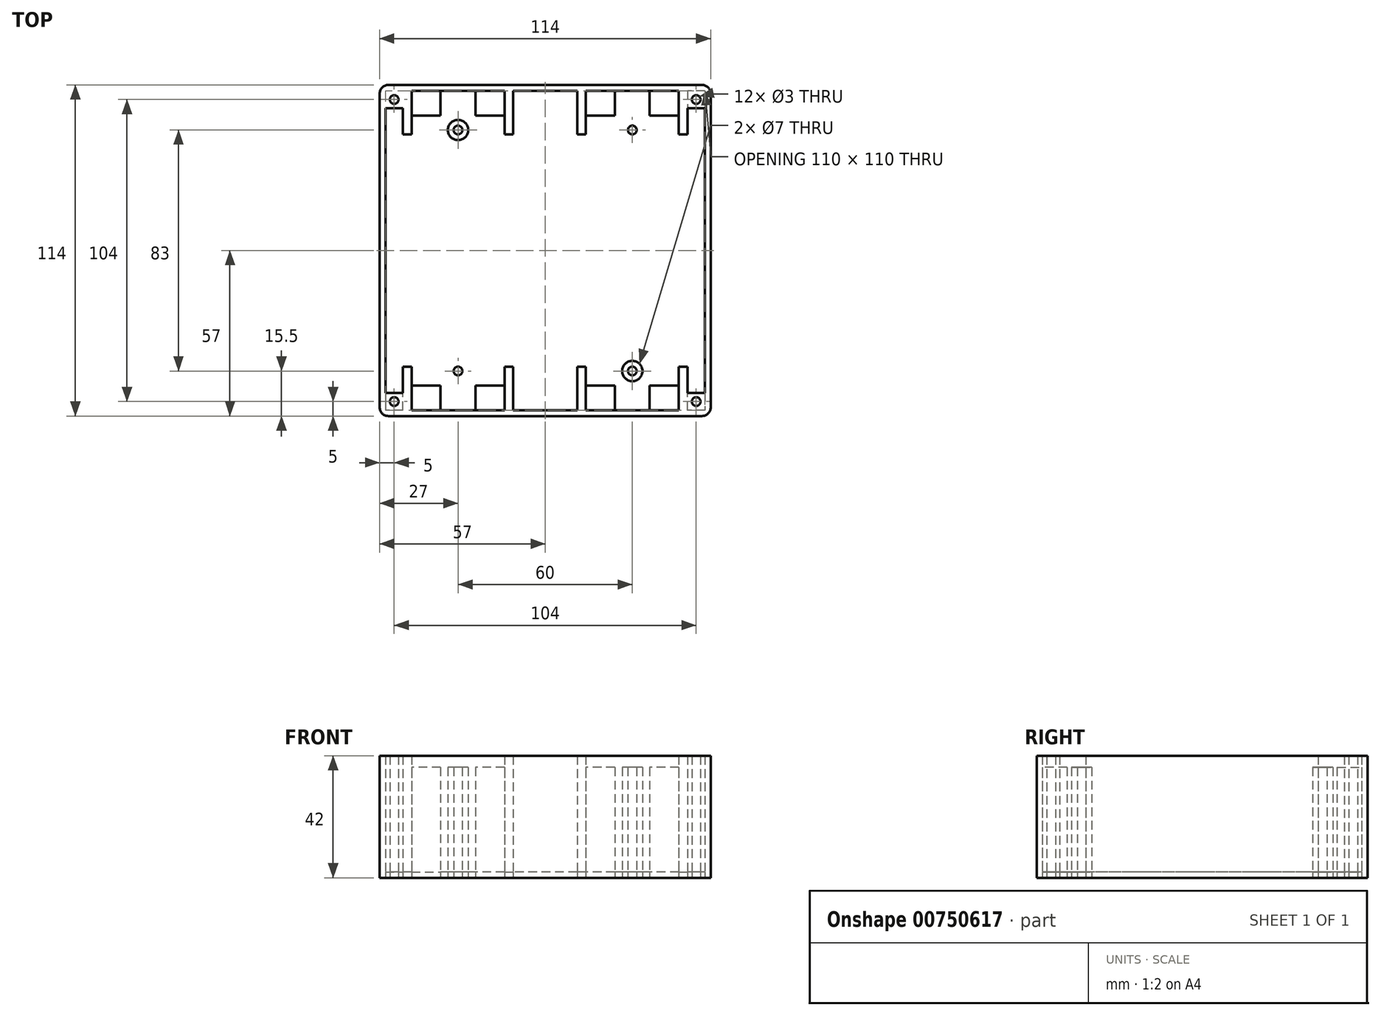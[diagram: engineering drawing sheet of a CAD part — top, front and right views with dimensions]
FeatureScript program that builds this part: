
annotation { "Feature Type Name" : "Feature", "Feature Type Description" : "" }
export const myFeature = defineFeature(function(context is Context, id is Id, definition is map)
    precondition{}
    {
        {
            var Q0;
            Q0=qCreatedBy(makeId("Top.planeOp"),FACE);
            var sketch = newSketch(context, id + "F0", { "sketchPlane" : qUnion([Q0])});
            skLineSegment(sketch, "E0.bottom", {"start": v(55, 55) * mm, "end": v(-55, 55) * mm});
            skLineSegment(sketch, "E0.top", {"start": v(55, -55) * mm, "end": v(-55, -55) * mm});
            skLineSegment(sketch, "E0.left", {"start": v(55, 55) * mm, "end": v(55, -55) * mm});
            skLineSegment(sketch, "E0.right", {"start": v(-55, 55) * mm, "end": v(-55, -55) * mm});
            skPoint(sketch, "E0.middle", {"position": v(0, 0) * mm});
            skLineSegment(sketch, "E1.bottom", {"start": v(57, -57) * mm, "end": v(-57, -57) * mm});
            skLineSegment(sketch, "E1.top", {"start": v(57, 57) * mm, "end": v(-57, 57) * mm});
            skLineSegment(sketch, "E1.left", {"start": v(57, -57) * mm, "end": v(57, 57) * mm});
            skLineSegment(sketch, "E1.right", {"start": v(-57, -57) * mm, "end": v(-57, 57) * mm});
            skLineSegment(sketch, "E2.bottom", {"start": v(-46, 46.5) * mm, "end": v(-36, 46.5) * mm});
            skLineSegment(sketch, "E2.top", {"start": v(-46, 55) * mm, "end": v(-14, 55) * mm});
            skLineSegment(sketch, "E2.left", {"start": v(-46, 46.5) * mm, "end": v(-46, 55) * mm});
            skLineSegment(sketch, "E2.right", {"start": v(-14, 46.5) * mm, "end": v(-14, 55) * mm});
            skLineSegment(sketch, "E3.MirrorCS", {"start": v(-46, -46.5) * mm, "end": v(-36, -46.5) * mm});
            skLineSegment(sketch, "E4.MirrorCS", {"start": v(-46, -46.5) * mm, "end": v(-46, -55) * mm});
            skLineSegment(sketch, "E5.MirrorCS", {"start": v(-14, -46.5) * mm, "end": v(-14, -55) * mm});
            skLineSegment(sketch, "E6.MirrorCS", {"start": v(14, 46.5) * mm, "end": v(14, 55) * mm});
            skLineSegment(sketch, "E7.MirrorCS", {"start": v(46, 46.5) * mm, "end": v(36, 46.5) * mm});
            skLineSegment(sketch, "E8.MirrorCS", {"start": v(46, 46.5) * mm, "end": v(46, 55) * mm});
            skLineSegment(sketch, "E9.MirrorCS", {"start": v(46, -46.5) * mm, "end": v(36, -46.5) * mm});
            skLineSegment(sketch, "E10.MirrorCS", {"start": v(14, -46.5) * mm, "end": v(14, -55) * mm});
            skLineSegment(sketch, "E11.MirrorCS", {"start": v(46, -46.5) * mm, "end": v(46, -55) * mm});
            skLineSegment(sketch, "E12.bottom", {"start": v(-46, 55) * mm, "end": v(-49, 55) * mm});
            skLineSegment(sketch, "E12.top", {"start": v(-46, 40) * mm, "end": v(-49, 40) * mm});
            skLineSegment(sketch, "E12.left", {"start": v(-46, 55) * mm, "end": v(-46, 40) * mm});
            skLineSegment(sketch, "E12.right", {"start": v(-49, 55) * mm, "end": v(-49, 40) * mm});
            skLineSegment(sketch, "E13.bottom", {"start": v(-14, 55) * mm, "end": v(-11, 55) * mm});
            skLineSegment(sketch, "E13.top", {"start": v(-14, 40) * mm, "end": v(-11, 40) * mm});
            skLineSegment(sketch, "E13.left", {"start": v(-14, 55) * mm, "end": v(-14, 40) * mm});
            skLineSegment(sketch, "E13.right", {"start": v(-11, 55) * mm, "end": v(-11, 40) * mm});
            skLineSegment(sketch, "E14.MirrorCS", {"start": v(11, 55) * mm, "end": v(11, 40) * mm});
            skLineSegment(sketch, "E15.MirrorCS", {"start": v(14, 40) * mm, "end": v(11, 40) * mm});
            skLineSegment(sketch, "E16.MirrorCS", {"start": v(14, 55) * mm, "end": v(14, 40) * mm});
            skLineSegment(sketch, "E17.MirrorCS", {"start": v(46, 55) * mm, "end": v(46, 40) * mm});
            skLineSegment(sketch, "E18.MirrorCS", {"start": v(46, 40) * mm, "end": v(49, 40) * mm});
            skLineSegment(sketch, "E19.MirrorCS", {"start": v(49, 55) * mm, "end": v(49, 40) * mm});
            skLineSegment(sketch, "E20.MirrorCS", {"start": v(-49, -55) * mm, "end": v(-49, -40) * mm});
            skLineSegment(sketch, "E21.MirrorCS", {"start": v(-46, -40) * mm, "end": v(-49, -40) * mm});
            skLineSegment(sketch, "E22.MirrorCS", {"start": v(-46, -55) * mm, "end": v(-46, -40) * mm});
            skLineSegment(sketch, "E23.MirrorCS", {"start": v(-14, -55) * mm, "end": v(-14, -40) * mm});
            skLineSegment(sketch, "E24.MirrorCS", {"start": v(-14, -40) * mm, "end": v(-11, -40) * mm});
            skLineSegment(sketch, "E25.MirrorCS", {"start": v(-11, -55) * mm, "end": v(-11, -40) * mm});
            skLineSegment(sketch, "E26.MirrorCS", {"start": v(11, -55) * mm, "end": v(11, -40) * mm});
            skLineSegment(sketch, "E27.MirrorCS", {"start": v(14, -40) * mm, "end": v(11, -40) * mm});
            skLineSegment(sketch, "E28.MirrorCS", {"start": v(14, -55) * mm, "end": v(14, -40) * mm});
            skLineSegment(sketch, "E29.MirrorCS", {"start": v(46, -55) * mm, "end": v(46, -40) * mm});
            skLineSegment(sketch, "E30.MirrorCS", {"start": v(46, -40) * mm, "end": v(49, -40) * mm});
            skLineSegment(sketch, "E31.MirrorCS", {"start": v(49, -55) * mm, "end": v(49, -40) * mm});
            skLineSegment(sketch, "E32.top", {"start": v(-46, 55) * mm, "end": v(-36, 55) * mm});
            skLineSegment(sketch, "E32.right", {"start": v(-36, 46.5) * mm, "end": v(-36, 55) * mm});
            skLineSegment(sketch, "E33.bottom", {"start": v(-14, 46.5) * mm, "end": v(-24, 46.5) * mm});
            skLineSegment(sketch, "E33.top", {"start": v(-14, 55) * mm, "end": v(-24, 55) * mm});
            skLineSegment(sketch, "E33.right", {"start": v(-24, 46.5) * mm, "end": v(-24, 55) * mm});
            skLineSegment(sketch, "E34.MirrorCS", {"start": v(36, 46.5) * mm, "end": v(36, 55) * mm});
            skLineSegment(sketch, "E35.MirrorCS", {"start": v(24, 46.5) * mm, "end": v(24, 55) * mm});
            skLineSegment(sketch, "E36.MirrorCS", {"start": v(-36, -46.5) * mm, "end": v(-36, -55) * mm});
            skLineSegment(sketch, "E37.MirrorCS", {"start": v(-24, -46.5) * mm, "end": v(-24, -55) * mm});
            skLineSegment(sketch, "E38.MirrorCS", {"start": v(24, -46.5) * mm, "end": v(24, -55) * mm});
            skLineSegment(sketch, "E39.MirrorCS", {"start": v(36, -46.5) * mm, "end": v(36, -55) * mm});
            skLineSegment(sketch, "E40.trimOffspring", {"start": v(-24, 46.5) * mm, "end": v(-14, 46.5) * mm});
            skLineSegment(sketch, "E41.trimOffspring", {"start": v(-24, -46.5) * mm, "end": v(-14, -46.5) * mm});
            skLineSegment(sketch, "E42.trimOffspring", {"start": v(24, -46.5) * mm, "end": v(14, -46.5) * mm});
            skLineSegment(sketch, "E43.trimOffspring", {"start": v(24, 46.5) * mm, "end": v(14, 46.5) * mm});
            skPoint(sketch, "E44", {"position": v(-30, 55) * mm});
            skPoint(sketch, "E45", {"position": v(-30, 41.5) * mm});
            skCircle(sketch, "E46", {"center": v(-30, 41.5) * mm, "radius": 1.5 * mm});
            skCircle(sketch, "E47", {"center": v(-30, 41.5) * mm, "radius": 3.5 * mm});
            skCircle(sketch, "E48.MirrorC", {"center": v(30, 41.5) * mm, "radius": 1.5 * mm});
            skCircle(sketch, "E49.MirrorC", {"center": v(30, 41.5) * mm, "radius": 3.5 * mm});
            skCircle(sketch, "E50.MirrorC", {"center": v(-30, -41.5) * mm, "radius": 1.5 * mm});
            skCircle(sketch, "E51.MirrorC", {"center": v(-30, -41.5) * mm, "radius": 3.5 * mm});
            skCircle(sketch, "E52.MirrorC", {"center": v(30, -41.5) * mm, "radius": 1.5 * mm});
            skCircle(sketch, "E53.MirrorC", {"center": v(30, -41.5) * mm, "radius": 3.5 * mm});
            skLineSegment(sketch, "E54", {"start": v(-55, 49) * mm, "end": v(-49, 49) * mm});
            skLineSegment(sketch, "E55.MirrorCS", {"start": v(55, 49) * mm, "end": v(49, 49) * mm});
            skLineSegment(sketch, "E56.MirrorCS", {"start": v(-55, -49) * mm, "end": v(-49, -49) * mm});
            skLineSegment(sketch, "E57.MirrorCS", {"start": v(55, -49) * mm, "end": v(49, -49) * mm});
            skPoint(sketch, "E58", {"position": v(-52, 52) * mm});
            skPoint(sketch, "E58.positionSnap0", {"position": v(-52, 49) * mm});
            skCircle(sketch, "E59", {"center": v(-52, 52) * mm, "radius": 1.5 * mm});
            skCircle(sketch, "E60.MirrorC", {"center": v(52, 52) * mm, "radius": 1.5 * mm});
            skCircle(sketch, "E61.MirrorC", {"center": v(-52, -52) * mm, "radius": 1.5 * mm});
            skCircle(sketch, "E62.MirrorC", {"center": v(52, -52) * mm, "radius": 1.5 * mm});
            skSolve(sketch);
        }
        {
            var Q0;
            Q0=makeQuery(id+"F0.imprint","IMPRINT",FACE,{"disambiguationData":[TD([[makeQuery(id+"F0.imprint","IMPRINT",EDGE,{"derivedFrom":sQuery(id+"F0.wireOp",EDGE,"E1.bottom")}),-1.0]])]});
            var Q1;
            {var subQ0=sQuery(id+"F0.wireOp",EDGE,"E2.right");Q1=makeQuery(id+"F0.imprint","IMPRINT",FACE,{"disambiguationData":[TD([[makeQuery(id+"F0.imprint","IMPRINT",EDGE,{"derivedFrom":subQ0}),-1.0]])]});}
            var Q2;
            {var subQ1=sQuery(id+"F0.wireOp",EDGE,"E6.MirrorCS");Q2=makeQuery(id+"F0.imprint","IMPRINT",FACE,{"disambiguationData":[TD([[makeQuery(id+"F0.imprint","IMPRINT",EDGE,{"derivedFrom":subQ1}),1.0]])]});}
            var Q3;
            {var subQ1=sQuery(id+"F0.wireOp",EDGE,"E8.MirrorCS");Q3=makeQuery(id+"F0.imprint","IMPRINT",FACE,{"disambiguationData":[TD([[makeQuery(id+"F0.imprint","IMPRINT",EDGE,{"derivedFrom":subQ1}),-1.0]])]});}
            var Q4;
            {var subQ1=sQuery(id+"F0.wireOp",EDGE,"E2.left");Q4=makeQuery(id+"F0.imprint","IMPRINT",FACE,{"disambiguationData":[TD([[makeQuery(id+"F0.imprint","IMPRINT",EDGE,{"derivedFrom":subQ1}),1.0]])]});}
            var Q5;
            {var subQ3=sQuery(id+"F0.wireOp",EDGE,"E4.MirrorCS");Q5=makeQuery(id+"F0.imprint","IMPRINT",FACE,{"disambiguationData":[TD([[makeQuery(id+"F0.imprint","IMPRINT",EDGE,{"derivedFrom":subQ3}),-1.0]])]});}
            var Q6;
            {var subQ0=sQuery(id+"F0.wireOp",EDGE,"E5.MirrorCS");Q6=makeQuery(id+"F0.imprint","IMPRINT",FACE,{"disambiguationData":[TD([[makeQuery(id+"F0.imprint","IMPRINT",EDGE,{"derivedFrom":subQ0}),1.0]])]});}
            var Q7;
            {var subQ1=sQuery(id+"F0.wireOp",EDGE,"E10.MirrorCS");Q7=makeQuery(id+"F0.imprint","IMPRINT",FACE,{"disambiguationData":[TD([[makeQuery(id+"F0.imprint","IMPRINT",EDGE,{"derivedFrom":subQ1}),-1.0]])]});}
            var Q8;
            {var subQ1=sQuery(id+"F0.wireOp",EDGE,"E11.MirrorCS");Q8=makeQuery(id+"F0.imprint","IMPRINT",FACE,{"disambiguationData":[TD([[makeQuery(id+"F0.imprint","IMPRINT",EDGE,{"derivedFrom":subQ1}),1.0]])]});}
            var Q9;
            {var subQ0=sQuery(id+"F0.wireOp",EDGE,"E54");Q9=makeQuery(id+"F0.imprint","IMPRINT",FACE,{"disambiguationData":[TD([[makeQuery(id+"F0.imprint","IMPRINT",EDGE,{"derivedFrom":subQ0}),1.0]])]});}
            var Q10;
            {var subQ0=sQuery(id+"F0.wireOp",EDGE,"E55.MirrorCS");Q10=makeQuery(id+"F0.imprint","IMPRINT",FACE,{"disambiguationData":[TD([[makeQuery(id+"F0.imprint","IMPRINT",EDGE,{"derivedFrom":subQ0}),-1.0]])]});}
            var Q11;
            {var subQ0=sQuery(id+"F0.wireOp",EDGE,"E57.MirrorCS");Q11=makeQuery(id+"F0.imprint","IMPRINT",FACE,{"disambiguationData":[TD([[makeQuery(id+"F0.imprint","IMPRINT",EDGE,{"derivedFrom":subQ0}),1.0]])]});}
            var Q12;
            {var subQ0=sQuery(id+"F0.wireOp",EDGE,"E56.MirrorCS");Q12=makeQuery(id+"F0.imprint","IMPRINT",FACE,{"disambiguationData":[TD([[makeQuery(id+"F0.imprint","IMPRINT",EDGE,{"derivedFrom":subQ0}),-1.0]])]});}
            extrude(context, id + "F1", {"entities" : qUnion([Q0, Q1, Q2, Q3, Q4, Q5, Q6, Q7, Q8, Q9, Q10, Q11, Q12]), "depth" : 42 * mm, "offsetDistance" : 25 * mm});
        }
        {
            var Q0;
            Q0=makeQuery(id+"F0.imprint","IMPRINT",FACE,{"disambiguationData":[TD([[makeQuery(id+"F0.imprint","IMPRINT",EDGE,{"derivedFrom":sQuery(id+"F0.wireOp",EDGE,"E2.bottom")}),1.0]])]});
            var Q1;
            Q1=makeQuery(id+"F0.imprint","IMPRINT",FACE,{"disambiguationData":[TD([[makeQuery(id+"F0.imprint","IMPRINT",EDGE,{"derivedFrom":sQuery(id+"F0.wireOp",EDGE,"E46")}),-1.0]])]});
            var Q2;
            {var subQ0=sQuery(id+"F0.wireOp",EDGE,"E2.right");Q2=makeQuery(id+"F0.imprint","IMPRINT",FACE,{"disambiguationData":[TD([[makeQuery(id+"F0.imprint","IMPRINT",EDGE,{"derivedFrom":subQ0}),1.0]])]});}
            var Q3;
            {var subQ0=sQuery(id+"F0.wireOp",EDGE,"E6.MirrorCS");Q3=makeQuery(id+"F0.imprint","IMPRINT",FACE,{"disambiguationData":[TD([[makeQuery(id+"F0.imprint","IMPRINT",EDGE,{"derivedFrom":subQ0}),-1.0]])]});}
            var Q4;
            Q4=makeQuery(id+"F0.imprint","IMPRINT",FACE,{"disambiguationData":[TD([[makeQuery(id+"F0.imprint","IMPRINT",EDGE,{"derivedFrom":sQuery(id+"F0.wireOp",EDGE,"E7.MirrorCS")}),-1.0]])]});
            var Q5;
            Q5=makeQuery(id+"F0.imprint","IMPRINT",FACE,{"disambiguationData":[TD([[makeQuery(id+"F0.imprint","IMPRINT",EDGE,{"derivedFrom":sQuery(id+"F0.wireOp",EDGE,"E48.MirrorC")}),1.0]])]});
            var Q6;
            Q6=makeQuery(id+"F0.imprint","IMPRINT",FACE,{"disambiguationData":[TD([[makeQuery(id+"F0.imprint","IMPRINT",EDGE,{"derivedFrom":sQuery(id+"F0.wireOp",EDGE,"E52.MirrorC")}),-1.0]])]});
            var Q7;
            Q7=makeQuery(id+"F0.imprint","IMPRINT",FACE,{"disambiguationData":[TD([[makeQuery(id+"F0.imprint","IMPRINT",EDGE,{"derivedFrom":sQuery(id+"F0.wireOp",EDGE,"E50.MirrorC")}),1.0]])]});
            var Q8;
            {var subQ0=sQuery(id+"F0.wireOp",EDGE,"E5.MirrorCS");Q8=makeQuery(id+"F0.imprint","IMPRINT",FACE,{"disambiguationData":[TD([[makeQuery(id+"F0.imprint","IMPRINT",EDGE,{"derivedFrom":subQ0}),-1.0]])]});}
            var Q9;
            Q9=makeQuery(id+"F0.imprint","IMPRINT",FACE,{"disambiguationData":[TD([[makeQuery(id+"F0.imprint","IMPRINT",EDGE,{"derivedFrom":sQuery(id+"F0.wireOp",EDGE,"E3.MirrorCS")}),-1.0]])]});
            var Q10;
            {var subQ0=sQuery(id+"F0.wireOp",EDGE,"E10.MirrorCS");Q10=makeQuery(id+"F0.imprint","IMPRINT",FACE,{"disambiguationData":[TD([[makeQuery(id+"F0.imprint","IMPRINT",EDGE,{"derivedFrom":subQ0}),1.0]])]});}
            var Q11;
            Q11=makeQuery(id+"F0.imprint","IMPRINT",FACE,{"disambiguationData":[TD([[makeQuery(id+"F0.imprint","IMPRINT",EDGE,{"derivedFrom":sQuery(id+"F0.wireOp",EDGE,"E9.MirrorCS")}),1.0]])]});
            extrude(context, id + "F2", {"entities" : qUnion([Q0, Q1, Q2, Q3, Q4, Q5, Q6, Q7, Q8, Q9, Q10, Q11]), "operationType" : NewBodyOperationType.ADD, "depth" : 38 * mm, "offsetDistance" : 25 * mm});
        }
        {
            var Q0;
            {var subQ0=sQuery(id+"F0.wireOp",EDGE,"E57.MirrorCS");var subQ6=sQuery(id+"F0.wireOp",EDGE,"E55.MirrorCS");Q0=qUnion([makeQuery(id+"F0.imprint","IMPRINT",FACE,{"disambiguationData":[TD([[makeQuery(id+"F0.imprint","IMPRINT",EDGE,{"derivedFrom":subQ6}),-1.0]])]}),makeQuery(id+"F0.imprint","IMPRINT",FACE,{"disambiguationData":[TD([[makeQuery(id+"F0.imprint","IMPRINT",EDGE,{"derivedFrom":subQ0}),1.0]])]})]);}
            extrude(context, id + "F3", {"entities" : qUnion([Q0]), "depth" : 2 * mm, "offsetDistance" : 25 * mm});
        }
        {
            var Q0;
            Q0=makeQuery(id+"F0.imprint","IMPRINT",FACE,{"disambiguationData":[TD([[makeQuery(id+"F0.imprint","IMPRINT",EDGE,{"derivedFrom":sQuery(id+"F0.wireOp",EDGE,"E59")}),1.0]])]});
            var Q1;
            Q1=makeQuery(id+"F0.imprint","IMPRINT",FACE,{"disambiguationData":[TD([[makeQuery(id+"F0.imprint","IMPRINT",EDGE,{"derivedFrom":sQuery(id+"F0.wireOp",EDGE,"E46")}),1.0]])]});
            var Q2;
            Q2=makeQuery(id+"F0.imprint","IMPRINT",FACE,{"disambiguationData":[TD([[makeQuery(id+"F0.imprint","IMPRINT",EDGE,{"derivedFrom":sQuery(id+"F0.wireOp",EDGE,"E2.bottom")}),-1.0]])]});
            var Q3;
            Q3=makeQuery(id+"F0.imprint","IMPRINT",FACE,{"disambiguationData":[TD([[makeQuery(id+"F0.imprint","IMPRINT",EDGE,{"derivedFrom":sQuery(id+"F0.wireOp",EDGE,"E48.MirrorC")}),-1.0]])]});
            var Q4;
            Q4=makeQuery(id+"F0.imprint","IMPRINT",FACE,{"disambiguationData":[TD([[makeQuery(id+"F0.imprint","IMPRINT",EDGE,{"derivedFrom":sQuery(id+"F0.wireOp",EDGE,"E60.MirrorC")}),-1.0]])]});
            var Q5;
            Q5=makeQuery(id+"F0.imprint","IMPRINT",FACE,{"disambiguationData":[TD([[makeQuery(id+"F0.imprint","IMPRINT",EDGE,{"derivedFrom":sQuery(id+"F0.wireOp",EDGE,"E61.MirrorC")}),-1.0]])]});
            var Q6;
            Q6=makeQuery(id+"F0.imprint","IMPRINT",FACE,{"disambiguationData":[TD([[makeQuery(id+"F0.imprint","IMPRINT",EDGE,{"derivedFrom":sQuery(id+"F0.wireOp",EDGE,"E50.MirrorC")}),-1.0]])]});
            var Q7;
            Q7=makeQuery(id+"F0.imprint","IMPRINT",FACE,{"disambiguationData":[TD([[makeQuery(id+"F0.imprint","IMPRINT",EDGE,{"derivedFrom":sQuery(id+"F0.wireOp",EDGE,"E52.MirrorC")}),1.0]])]});
            var Q8;
            Q8=makeQuery(id+"F0.imprint","IMPRINT",FACE,{"disambiguationData":[TD([[makeQuery(id+"F0.imprint","IMPRINT",EDGE,{"derivedFrom":sQuery(id+"F0.wireOp",EDGE,"E62.MirrorC")}),1.0]])]});
            extrude(context, id + "F4", {"entities" : qUnion([Q0, Q1, Q2, Q3, Q4, Q5, Q6, Q7, Q8]), "depth" : 2 * mm, "offsetDistance" : 25 * mm});
        }
        {
            var Q0;
            Q0=makeQuery(id+"F1.opExtrude","SWEPT_EDGE",EDGE,{"disambiguationData":[OSD([sQuery(id+"F0.wireOp",EDGE,"E1.top"),sQuery(id+"F0.wireOp",EDGE,"E1.right")])]});
            var Q1;
            Q1=makeQuery(id+"F1.opExtrude","SWEPT_EDGE",EDGE,{"disambiguationData":[OSD([sQuery(id+"F0.wireOp",EDGE,"E1.top"),sQuery(id+"F0.wireOp",EDGE,"E1.left")])]});
            var Q2;
            Q2=makeQuery(id+"F1.opExtrude","SWEPT_EDGE",EDGE,{"disambiguationData":[OSD([sQuery(id+"F0.wireOp",EDGE,"E1.bottom"),sQuery(id+"F0.wireOp",EDGE,"E1.right")])]});
            var Q3;
            Q3=makeQuery(id+"F1.opExtrude","SWEPT_EDGE",EDGE,{"disambiguationData":[OSD([sQuery(id+"F0.wireOp",EDGE,"E1.bottom"),sQuery(id+"F0.wireOp",EDGE,"E1.left")])]});
            fillet(context, id + "F5", {"entities" : qUnion([Q0, Q1, Q2, Q3]), "radius" : 3 * mm, "tangentPropagation" : true, "allowEdgeOverflow" : false});
        }
    });
